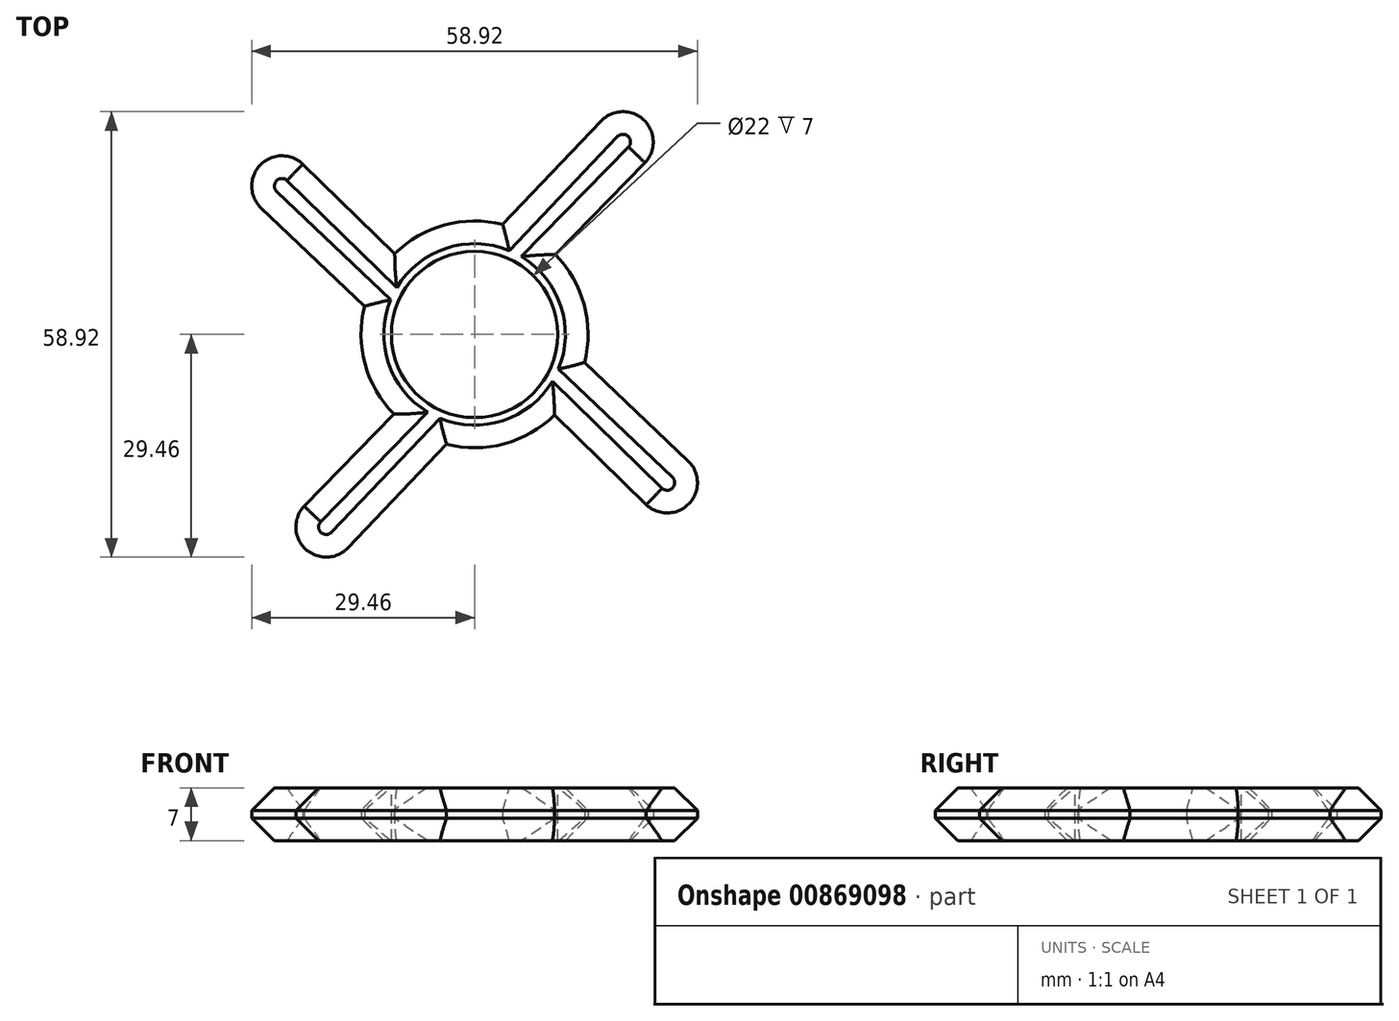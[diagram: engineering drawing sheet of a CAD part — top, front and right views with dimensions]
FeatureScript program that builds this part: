
annotation { "Feature Type Name" : "Feature", "Feature Type Description" : "" }
export const myFeature = defineFeature(function(context is Context, id is Id, definition is map)
    precondition{}
    {
        {
            var Q0;
            Q0=qCreatedBy(makeId("Top.planeOp"),FACE);
            var sketch = newSketch(context, id + "F0", { "sketchPlane" : qUnion([Q0])});
            skCircle(sketch, "E0", {"center": v(0, 0) * mm, "radius": 15 * mm});
            skLineSegment(sketch, "E1", {"start": v(3.72, 14.53) * mm, "end": v(16.72, 28.22) * mm});
            skLineSegment(sketch, "E2", {"start": v(10.66, 10.56) * mm, "end": v(22.52, 22.7) * mm});
            skArc(sketch, "E3", {"start": v(22.52, 22.7) * mm, "mid": v(22.38, 28.36) * mm, "end": v(16.72, 28.22) * mm});
            skLineSegment(sketch, "E4.1.0", {"start": v(-14.53, 3.72) * mm, "end": v(-28.22, 16.72) * mm});
            skArc(sketch, "E4.1.1", {"start": v(-22.7, 22.52) * mm, "mid": v(-28.36, 22.38) * mm, "end": v(-28.22, 16.72) * mm});
            skLineSegment(sketch, "E4.1.2", {"start": v(-10.56, 10.66) * mm, "end": v(-22.7, 22.52) * mm});
            skLineSegment(sketch, "E4.2.0", {"start": v(-3.72, -14.53) * mm, "end": v(-16.72, -28.22) * mm});
            skArc(sketch, "E4.2.1", {"start": v(-22.52, -22.7) * mm, "mid": v(-22.38, -28.36) * mm, "end": v(-16.72, -28.22) * mm});
            skLineSegment(sketch, "E4.2.2", {"start": v(-10.66, -10.56) * mm, "end": v(-22.52, -22.7) * mm});
            skLineSegment(sketch, "E5.1.3.0", {"start": v(14.53, -3.72) * mm, "end": v(28.22, -16.72) * mm});
            skArc(sketch, "E5.3.3.0", {"start": v(22.7, -22.52) * mm, "mid": v(28.36, -22.38) * mm, "end": v(28.22, -16.72) * mm});
            skLineSegment(sketch, "E5.7.3.0", {"start": v(10.56, -10.66) * mm, "end": v(22.7, -22.52) * mm});
            skSolve(sketch);
        }
        {
            var Q0;
            {var subQ0=sQuery(id+"F0.wireOp",EDGE,"E4.1.0");Q0=makeQuery(id+"F0.imprint","IMPRINT",FACE,{"disambiguationData":[TD([[makeQuery(id+"F0.imprint","IMPRINT",EDGE,{"derivedFrom":subQ0}),-1.0]])]});}
            var Q1;
            {var subQ0=sQuery(id+"F0.wireOp",EDGE,"E0");var subQ4=makeQuery(id+"F0.imprint","INTERSECT",VERTEX,{"derivedFrom":[subQ0,sQuery(id+"F0.wireOp",EDGE,"E1")]});Q1=makeQuery(id+"F0.imprint","IMPRINT",FACE,{"disambiguationData":[TD([[makeQuery(id+"F0.imprint","IMPRINT",EDGE,{"disambiguationData":[TD([[subQ4,1.0]])],"derivedFrom":subQ0}),1.0]])]});}
            var Q2;
            {var subQ0=sQuery(id+"F0.wireOp",EDGE,"E1");Q2=makeQuery(id+"F0.imprint","IMPRINT",FACE,{"disambiguationData":[TD([[makeQuery(id+"F0.imprint","IMPRINT",EDGE,{"derivedFrom":subQ0}),-1.0]])]});}
            var Q3;
            {var subQ0=sQuery(id+"F0.wireOp",EDGE,"E4.2.0");Q3=makeQuery(id+"F0.imprint","IMPRINT",FACE,{"disambiguationData":[TD([[makeQuery(id+"F0.imprint","IMPRINT",EDGE,{"derivedFrom":subQ0}),-1.0]])]});}
            extrude(context, id + "F1", {"entities" : qUnion([Q0, Q1, Q2, Q3]), "depth" : 7 * mm, "offsetDistance" : 25 * mm});
        }
        {
            var Q0;
            Q0=makeQuery(id+"F1.opExtrude","CAP_FACE",FACE,{"disambiguationData":[OSD([sQuery(id+"F0.wireOp",EDGE,"E0"),sQuery(id+"F0.wireOp",EDGE,"E1"),sQuery(id+"F0.wireOp",EDGE,"E2"),sQuery(id+"F0.wireOp",EDGE,"E3"),sQuery(id+"F0.wireOp",EDGE,"E4.1.0"),sQuery(id+"F0.wireOp",EDGE,"E4.1.1"),sQuery(id+"F0.wireOp",EDGE,"E4.1.2"),sQuery(id+"F0.wireOp",EDGE,"E4.2.0"),sQuery(id+"F0.wireOp",EDGE,"E4.2.1"),sQuery(id+"F0.wireOp",EDGE,"E4.2.2")])],"isStart":false});
            var sketch = newSketch(context, id + "F2", { "sketchPlane" : qUnion([Q0])});
            skCircle(sketch, "E6", {"center": v(0, 0) * mm, "radius": 11 * mm});
            skSolve(sketch);
        }
        {
            var Q0;
            Q0 = qSketchRegion(id + "F2", true);
            extrude(context, id + "F3", {"entities" : qUnion([Q0]), "operationType" : NewBodyOperationType.REMOVE, "oppositeDirection" : true, "depth" : 25 * mm, "offsetDistance" : 25 * mm});
        }
        {
            var Q0;
            {var subQ0=sQuery(id+"F0.wireOp",EDGE,"E5.1.3.0");Q0=makeQuery(id+"F0.imprint","IMPRINT",FACE,{"disambiguationData":[TD([[makeQuery(id+"F0.imprint","IMPRINT",EDGE,{"derivedFrom":subQ0}),-1.0]])]});}
            var Q1;
            Q1=sQuery(id+"F0.wireOp",EDGE,"E5.7.3.0");
            var Q2;
            Q2=sQuery(id+"F0.wireOp",EDGE,"E5.1.3.0");
            var Q3;
            Q3=sQuery(id+"F0.wireOp",EDGE,"E5.3.3.0");
            extrude(context, id + "F4", {"entities" : qUnion([Q0]), "operationType" : NewBodyOperationType.ADD, "surfaceEntities" : qUnion([Q1, Q2, Q3]), "depth" : 7 * mm, "offsetDistance" : 25 * mm});
        }
        {
            var Q0;
            Q0=makeQuery(id+"F1.opExtrude","CAP_EDGE",EDGE,{"disambiguationData":[OSD([sQuery(id+"F0.wireOp",EDGE,"E2")])],"isStart":false});
            var Q1;
            Q1=makeQuery(id+"F1.opExtrude","CAP_EDGE",EDGE,{"disambiguationData":[OSD([sQuery(id+"F0.wireOp",EDGE,"E4.1.2")])],"isStart":false});
            var Q2;
            Q2=makeQuery(id+"F1.opExtrude","CAP_EDGE",EDGE,{"disambiguationData":[OSD([sQuery(id+"F0.wireOp",EDGE,"E4.2.2")])],"isStart":false});
            var Q3;
            Q3=makeQuery(id+"F4.opExtrude","CAP_EDGE",EDGE,{"disambiguationData":[OSD([sQuery(id+"F0.wireOp",EDGE,"E5.7.3.0")])],"isStart":false});
            chamfer(context, id + "F5", {"entities" : qUnion([Q0, Q1, Q2, Q3]), "width" : 3 * mm, "tangentPropagation" : true});
        }
        {
            var Q0;
            Q0=makeQuery(id+"F1.opExtrude","CAP_EDGE",EDGE,{"disambiguationData":[OSD([sQuery(id+"F0.wireOp",EDGE,"E1")])],"isStart":false});
            var Q1;
            Q1=makeQuery(id+"F1.opExtrude","CAP_EDGE",EDGE,{"disambiguationData":[OSD([sQuery(id+"F0.wireOp",EDGE,"E4.1.0")])],"isStart":false});
            var Q2;
            Q2=makeQuery(id+"F1.opExtrude","CAP_EDGE",EDGE,{"disambiguationData":[OSD([sQuery(id+"F0.wireOp",EDGE,"E4.2.0")])],"isStart":false});
            var Q3;
            Q3=makeQuery(id+"F4.opExtrude","CAP_EDGE",EDGE,{"disambiguationData":[OSD([sQuery(id+"F0.wireOp",EDGE,"E5.1.3.0")])],"isStart":false});
            var Q4;
            Q4=makeQuery(id+"F4.opExtrude","CAP_EDGE",EDGE,{"disambiguationData":[OSD([sQuery(id+"F0.wireOp",EDGE,"E5.3.3.0")])],"isStart":false});
            var Q5;
            Q5=makeQuery(id+"F1.opExtrude","CAP_EDGE",EDGE,{"disambiguationData":[OSD([sQuery(id+"F0.wireOp",EDGE,"E4.2.1")])],"isStart":false});
            var Q6;
            Q6=makeQuery(id+"F1.opExtrude","CAP_EDGE",EDGE,{"disambiguationData":[OSD([sQuery(id+"F0.wireOp",EDGE,"E4.1.1")])],"isStart":false});
            var Q7;
            Q7=makeQuery(id+"F1.opExtrude","CAP_EDGE",EDGE,{"disambiguationData":[OSD([sQuery(id+"F0.wireOp",EDGE,"E3")])],"isStart":false});
            chamfer(context, id + "F6", {"entities" : qUnion([Q0, Q1, Q2, Q3, Q4, Q5, Q6, Q7]), "width" : 3 * mm, "tangentPropagation" : true});
        }
        {
            var Q0;
            Q0=makeQuery(id+"F4.opExtrude","CAP_EDGE",EDGE,{"disambiguationData":[OSD([sQuery(id+"F0.wireOp",EDGE,"E5.7.3.0")])],"isStart":true});
            var Q1;
            {var subQ0=sQuery(id+"F0.wireOp",EDGE,"E2");var subQ1=sQuery(id+"F0.wireOp",EDGE,"E0");var subQ2=sQuery(id+"F0.wireOp",EDGE,"E5.1.3.0");var subQ3=makeQuery(id+"F0.imprint","INTERSECT",VERTEX,{"derivedFrom":[subQ1,subQ2]});var subQ4=makeQuery(id+"F0.imprint","IMPRINT",EDGE,{"disambiguationData":[TD([[makeQuery(id+"F0.imprint","INTERSECT",VERTEX,{"derivedFrom":[subQ1,subQ0]}),1.0]])],"derivedFrom":subQ1});var subQ7=makeQuery(id+"F0.imprint","IMPRINT",EDGE,{"disambiguationData":[TD([[subQ3,1.0]])],"derivedFrom":subQ1});var subQ8=sQuery(id+"F0.wireOp",EDGE,"E4.2.0");var subQ9=makeQuery(id+"F0.imprint","IMPRINT",EDGE,{"disambiguationData":[TD([[makeQuery(id+"F0.imprint","INTERSECT",VERTEX,{"derivedFrom":[subQ1,subQ8]}),-1.0]])],"derivedFrom":subQ1});Q1=makeQuery(id+"F4.boolean.opBoolean","SPLIT",EDGE,{"disambiguationData":[TD([makeQuery(id+"F1.opExtrude","SWEPT_FACE",FACE,{"disambiguationData":[OSD([subQ8])]})])],"derivedFrom":makeQuery(id+"F1.opExtrude","CAP_EDGE",EDGE,{"disambiguationData":[OSD([subQ1]),TDD([subQ9,subQ7,subQ4])],"isStart":true})});}
            var Q2;
            Q2=makeQuery(id+"F1.opExtrude","CAP_EDGE",EDGE,{"disambiguationData":[OSD([sQuery(id+"F0.wireOp",EDGE,"E4.2.0")])],"isStart":true});
            var Q3;
            Q3=makeQuery(id+"F1.opExtrude","CAP_EDGE",EDGE,{"disambiguationData":[OSD([sQuery(id+"F0.wireOp",EDGE,"E4.2.2")])],"isStart":true});
            var Q4;
            {var subQ0=sQuery(id+"F0.wireOp",EDGE,"E0");Q4=makeQuery(id+"F1.opExtrude","CAP_EDGE",EDGE,{"disambiguationData":[OSD([subQ0]),TDD([makeQuery(id+"F0.imprint","IMPRINT",EDGE,{"disambiguationData":[TD([[makeQuery(id+"F0.imprint","INTERSECT",VERTEX,{"derivedFrom":[subQ0,sQuery(id+"F0.wireOp",EDGE,"E4.1.0")]}),-1.0]])],"derivedFrom":subQ0})])],"isStart":true});}
            var Q5;
            Q5=makeQuery(id+"F1.opExtrude","CAP_EDGE",EDGE,{"disambiguationData":[OSD([sQuery(id+"F0.wireOp",EDGE,"E4.1.0")])],"isStart":true});
            var Q6;
            Q6=makeQuery(id+"F1.opExtrude","CAP_EDGE",EDGE,{"disambiguationData":[OSD([sQuery(id+"F0.wireOp",EDGE,"E4.1.2")])],"isStart":true});
            var Q7;
            Q7=makeQuery(id+"F1.opExtrude","CAP_EDGE",EDGE,{"disambiguationData":[OSD([sQuery(id+"F0.wireOp",EDGE,"E4.1.1")])],"isStart":true});
            var Q8;
            Q8=makeQuery(id+"F1.opExtrude","CAP_EDGE",EDGE,{"disambiguationData":[OSD([sQuery(id+"F0.wireOp",EDGE,"E1")])],"isStart":true});
            var Q9;
            Q9=makeQuery(id+"F1.opExtrude","CAP_EDGE",EDGE,{"disambiguationData":[OSD([sQuery(id+"F0.wireOp",EDGE,"E2")])],"isStart":true});
            var Q10;
            Q10=makeQuery(id+"F1.opExtrude","CAP_EDGE",EDGE,{"disambiguationData":[OSD([sQuery(id+"F0.wireOp",EDGE,"E3")])],"isStart":true});
            var Q11;
            Q11=makeQuery(id+"F4.opExtrude","CAP_EDGE",EDGE,{"disambiguationData":[OSD([sQuery(id+"F0.wireOp",EDGE,"E5.3.3.0")])],"isStart":true});
            var Q12;
            Q12=makeQuery(id+"F4.opExtrude","CAP_EDGE",EDGE,{"disambiguationData":[OSD([sQuery(id+"F0.wireOp",EDGE,"E5.1.3.0")])],"isStart":true});
            var Q13;
            Q13=makeQuery(id+"F1.opExtrude","CAP_EDGE",EDGE,{"disambiguationData":[OSD([sQuery(id+"F0.wireOp",EDGE,"E4.2.1")])],"isStart":true});
            var Q14;
            {var subQ0=sQuery(id+"F0.wireOp",EDGE,"E0");Q14=makeQuery(id+"F1.opExtrude","CAP_EDGE",EDGE,{"disambiguationData":[OSD([subQ0]),TDD([makeQuery(id+"F0.imprint","IMPRINT",EDGE,{"disambiguationData":[TD([[makeQuery(id+"F0.imprint","INTERSECT",VERTEX,{"derivedFrom":[subQ0,sQuery(id+"F0.wireOp",EDGE,"E1")]}),-1.0]])],"derivedFrom":subQ0})])],"isStart":true});}
            var Q15;
            {var subQ0=sQuery(id+"F0.wireOp",EDGE,"E2");var subQ1=sQuery(id+"F0.wireOp",EDGE,"E0");var subQ2=sQuery(id+"F0.wireOp",EDGE,"E5.1.3.0");var subQ3=makeQuery(id+"F0.imprint","INTERSECT",VERTEX,{"derivedFrom":[subQ1,subQ2]});var subQ4=makeQuery(id+"F0.imprint","IMPRINT",EDGE,{"disambiguationData":[TD([[makeQuery(id+"F0.imprint","INTERSECT",VERTEX,{"derivedFrom":[subQ1,subQ0]}),1.0]])],"derivedFrom":subQ1});var subQ7=makeQuery(id+"F0.imprint","IMPRINT",EDGE,{"disambiguationData":[TD([[subQ3,1.0]])],"derivedFrom":subQ1});var subQ8=sQuery(id+"F0.wireOp",EDGE,"E4.2.0");var subQ9=makeQuery(id+"F0.imprint","IMPRINT",EDGE,{"disambiguationData":[TD([[makeQuery(id+"F0.imprint","INTERSECT",VERTEX,{"derivedFrom":[subQ1,subQ8]}),-1.0]])],"derivedFrom":subQ1});Q15=makeQuery(id+"F4.boolean.opBoolean","SPLIT",EDGE,{"disambiguationData":[TD([makeQuery(id+"F1.opExtrude","SWEPT_FACE",FACE,{"disambiguationData":[OSD([subQ0])]})])],"derivedFrom":makeQuery(id+"F1.opExtrude","CAP_EDGE",EDGE,{"disambiguationData":[OSD([subQ1]),TDD([subQ9,subQ7,subQ4])],"isStart":true})});}
            var Q16;
            {var subQ0=sQuery(id+"F0.wireOp",EDGE,"E2");var subQ1=sQuery(id+"F0.wireOp",EDGE,"E0");var subQ2=sQuery(id+"F0.wireOp",EDGE,"E5.1.3.0");var subQ3=makeQuery(id+"F0.imprint","INTERSECT",VERTEX,{"derivedFrom":[subQ1,subQ2]});var subQ4=makeQuery(id+"F0.imprint","IMPRINT",EDGE,{"disambiguationData":[TD([[makeQuery(id+"F0.imprint","INTERSECT",VERTEX,{"derivedFrom":[subQ1,subQ0]}),1.0]])],"derivedFrom":subQ1});var subQ7=makeQuery(id+"F0.imprint","IMPRINT",EDGE,{"disambiguationData":[TD([[subQ3,1.0]])],"derivedFrom":subQ1});var subQ8=sQuery(id+"F0.wireOp",EDGE,"E4.2.0");var subQ9=makeQuery(id+"F0.imprint","IMPRINT",EDGE,{"disambiguationData":[TD([[makeQuery(id+"F0.imprint","INTERSECT",VERTEX,{"derivedFrom":[subQ1,subQ8]}),-1.0]])],"derivedFrom":subQ1});Q16=makeQuery(id+"F4.boolean.opBoolean","SPLIT",EDGE,{"disambiguationData":[TD([makeQuery(id+"F1.opExtrude","SWEPT_FACE",FACE,{"disambiguationData":[OSD([subQ0])]})])],"derivedFrom":makeQuery(id+"F1.opExtrude","CAP_EDGE",EDGE,{"disambiguationData":[OSD([subQ1]),TDD([subQ9,subQ7,subQ4])],"isStart":false})});}
            var Q17;
            {var subQ0=sQuery(id+"F0.wireOp",EDGE,"E4.2.0");var subQ2=sQuery(id+"F0.wireOp",EDGE,"E5.1.3.0");var subQ3=sQuery(id+"F0.wireOp",EDGE,"E0");var subQ4=sQuery(id+"F0.wireOp",EDGE,"E2");var subQ5=makeQuery(id+"F0.imprint","INTERSECT",VERTEX,{"derivedFrom":[subQ3,subQ2]});var subQ6=makeQuery(id+"F0.imprint","IMPRINT",EDGE,{"disambiguationData":[TD([[makeQuery(id+"F0.imprint","INTERSECT",VERTEX,{"derivedFrom":[subQ3,subQ4]}),1.0]])],"derivedFrom":subQ3});var subQ8=makeQuery(id+"F0.imprint","IMPRINT",EDGE,{"disambiguationData":[TD([[subQ5,1.0]])],"derivedFrom":subQ3});var subQ9=makeQuery(id+"F0.imprint","IMPRINT",EDGE,{"disambiguationData":[TD([[makeQuery(id+"F0.imprint","INTERSECT",VERTEX,{"derivedFrom":[subQ3,subQ0]}),-1.0]])],"derivedFrom":subQ3});Q17=makeQuery(id+"F4.boolean.opBoolean","SPLIT",EDGE,{"disambiguationData":[TD([makeQuery(id+"F1.opExtrude","SWEPT_FACE",FACE,{"disambiguationData":[OSD([subQ0])]})])],"derivedFrom":makeQuery(id+"F1.opExtrude","CAP_EDGE",EDGE,{"disambiguationData":[OSD([subQ3]),TDD([subQ9,subQ8,subQ6])],"isStart":false})});}
            var Q18;
            {var subQ0=sQuery(id+"F0.wireOp",EDGE,"E0");Q18=makeQuery(id+"F1.opExtrude","CAP_EDGE",EDGE,{"disambiguationData":[OSD([subQ0]),TDD([makeQuery(id+"F0.imprint","IMPRINT",EDGE,{"disambiguationData":[TD([[makeQuery(id+"F0.imprint","INTERSECT",VERTEX,{"derivedFrom":[subQ0,sQuery(id+"F0.wireOp",EDGE,"E4.1.0")]}),-1.0]])],"derivedFrom":subQ0})])],"isStart":false});}
            var Q19;
            {var subQ0=sQuery(id+"F0.wireOp",EDGE,"E0");Q19=makeQuery(id+"F1.opExtrude","CAP_EDGE",EDGE,{"disambiguationData":[OSD([subQ0]),TDD([makeQuery(id+"F0.imprint","IMPRINT",EDGE,{"disambiguationData":[TD([[makeQuery(id+"F0.imprint","INTERSECT",VERTEX,{"derivedFrom":[subQ0,sQuery(id+"F0.wireOp",EDGE,"E1")]}),-1.0]])],"derivedFrom":subQ0})])],"isStart":false});}
            chamfer(context, id + "F7", {"entities" : qUnion([Q0, Q1, Q2, Q3, Q4, Q5, Q6, Q7, Q8, Q9, Q10, Q11, Q12, Q13, Q14, Q15, Q16, Q17, Q18, Q19]), "width" : 3 * mm, "tangentPropagation" : true});
        }
    });
